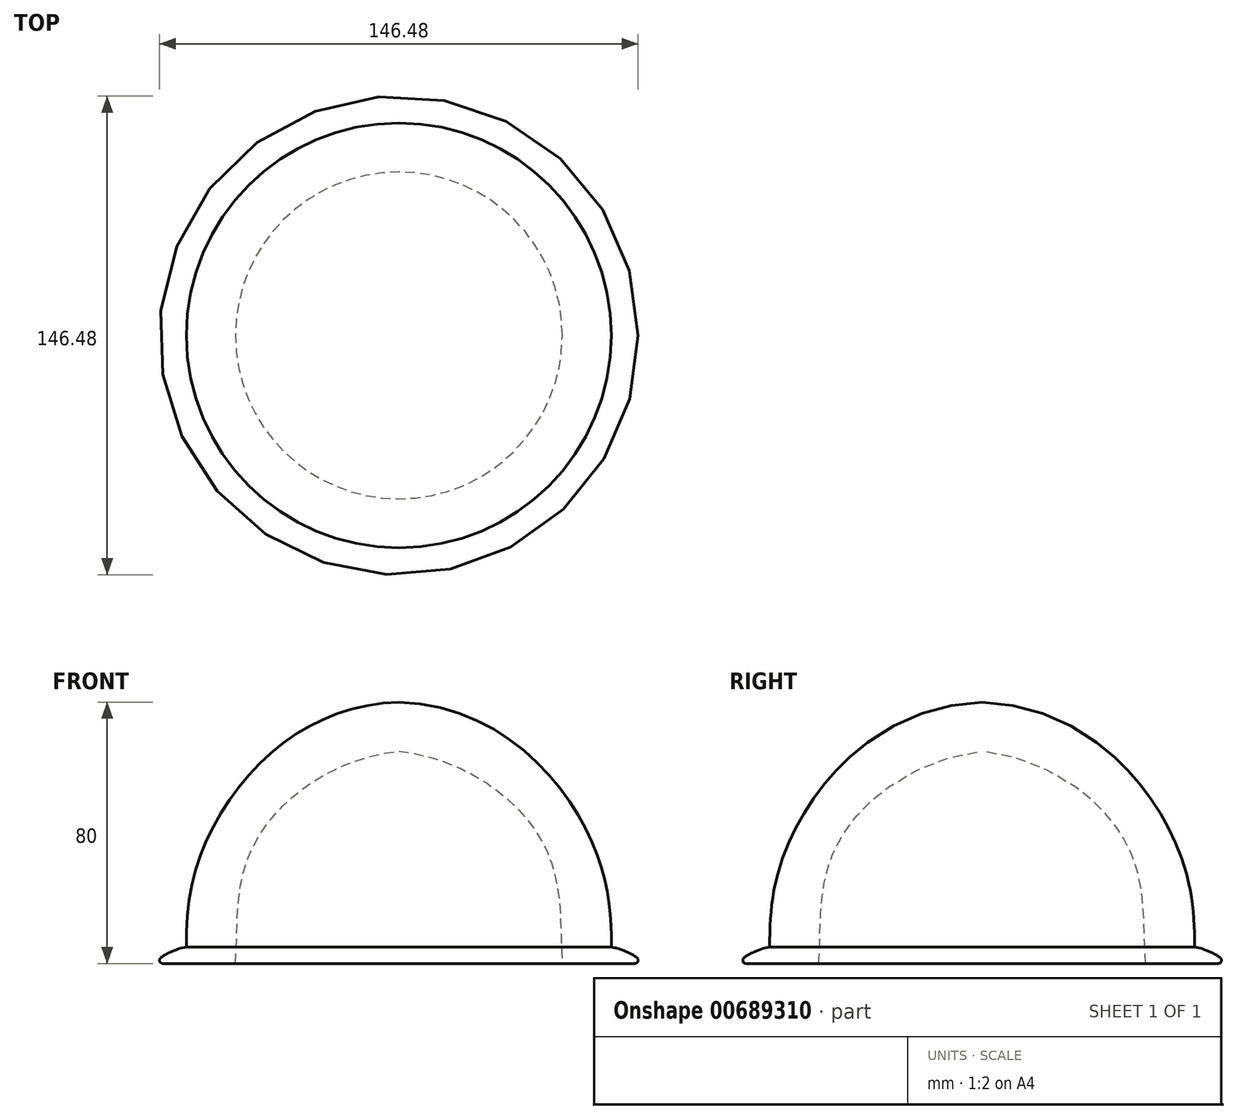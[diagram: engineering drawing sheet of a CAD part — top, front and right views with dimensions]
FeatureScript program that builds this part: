
annotation { "Feature Type Name" : "Feature", "Feature Type Description" : "" }
export const myFeature = defineFeature(function(context is Context, id is Id, definition is map)
    precondition{}
    {
        {
            var Q0;
            Q0=qCreatedBy(makeId("Front.planeOp"),FACE);
            var sketch = newSketch(context, id + "F0", { "sketchPlane" : qUnion([Q0])});
            skFitSpline(sketch, "E0", {"points": [v(0, 45) * mm, v(60, 0) * mm, v(65, -35) * mm], "startDerivative": vector(164.87, -5.9) * mm, "endDerivative": vector(-0.33, -81.9) * mm});
            skLineSegment(sketch, "E1", {"start": v(0, 45) * mm, "end": v(0, 30) * mm});
            skLineSegment(sketch, "E2", {"start": v(65, -35) * mm, "end": v(50, -35) * mm});
            skFitSpline(sketch, "E3", {"points": [v(0, 30) * mm, v(45, 0) * mm, v(50, -35) * mm], "startDerivative": vector(117.37, -13.4) * mm, "endDerivative": vector(5.28, -78.57) * mm});
            skLineSegment(sketch, "E4", {"start": v(65, -35) * mm, "end": v(75, -35) * mm});
            skFitSpline(sketch, "E5", {"points": [v(75, -35) * mm, v(69.87, -31.5) * mm, v(65.02, -30) * mm], "startDerivative": vector(-14.46, 13.18) * mm, "endDerivative": vector(-14.84, 2.2) * mm});
            skLineSegment(sketch, "E6", {"start": v(0, 30) * mm, "end": v(0, -35) * mm, "construction": true});
            skLineSegment(sketch, "E7", {"start": v(0, -35) * mm, "end": v(50, -35) * mm, "construction": true});
            skSolve(sketch);
        }
        {
            var Q0;
            {var subQ1=sQuery(id+"F0.wireOp",EDGE,"E1");Q0=makeQuery(id+"F0.imprint","IMPRINT",FACE,{"disambiguationData":[TD([[makeQuery(id+"F0.imprint","IMPRINT",EDGE,{"derivedFrom":subQ1}),1.0]])]});}
            var Q1;
            {var subQ0=sQuery(id+"F0.wireOp",EDGE,"E4");Q1=makeQuery(id+"F0.imprint","IMPRINT",FACE,{"disambiguationData":[TD([[makeQuery(id+"F0.imprint","IMPRINT",EDGE,{"derivedFrom":subQ0}),1.0]])]});}
            var Q2;
            Q2=sQuery(id+"F0.wireOp",EDGE,"E6");
            revolve(context, id + "F1", {"surfaceOperationType" : NewSurfaceOperationType.NEW, "entities" : qUnion([Q0, Q1]), "axis" : qUnion([Q2]), "revolveType" : RevolveType.FULL});
        }
        {
            var Q0;
            Q0=makeQuery(id+"F1.opRevolve","SWEPT_EDGE",EDGE,{"disambiguationData":[OSD([sQuery(id+"F0.wireOp",EDGE,"E4"),sQuery(id+"F0.wireOp",EDGE,"E5")])]});
            fillet(context, id + "F2", {"entities" : qUnion([Q0]), "radius" : 1 * mm, "tangentPropagation" : true, "allowEdgeOverflow" : false});
        }
    });
